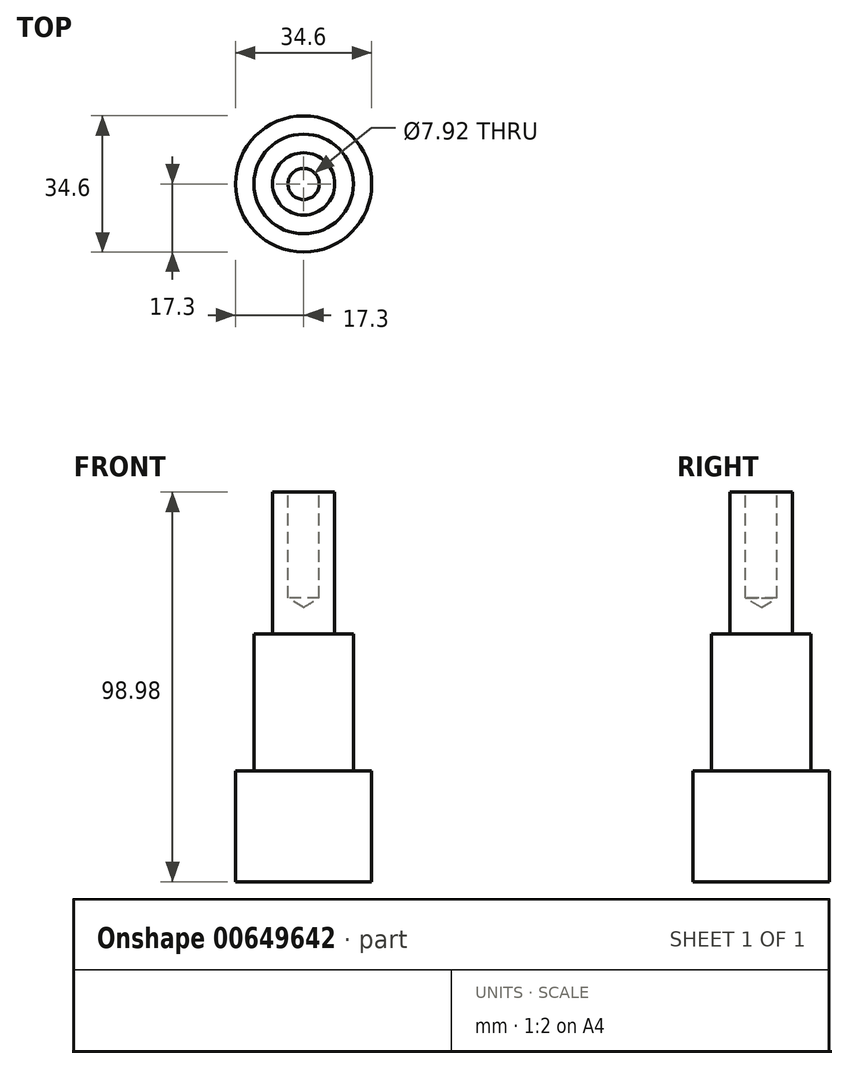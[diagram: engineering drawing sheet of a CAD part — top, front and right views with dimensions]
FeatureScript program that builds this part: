
annotation { "Feature Type Name" : "Feature", "Feature Type Description" : "" }
export const myFeature = defineFeature(function(context is Context, id is Id, definition is map)
    precondition{}
    {
        {
            var Q0;
            Q0=qCreatedBy(makeId("Top.planeOp"),FACE);
            var sketch = newSketch(context, id + "F0", { "sketchPlane" : qUnion([Q0])});
            skCircle(sketch, "E0", {"center": v(0, 0) * mm, "radius": 17.3 * mm});
            skSolve(sketch);
        }
        {
            var Q0;
            Q0=makeQuery(id+"F0.imprint","IMPRINT",FACE,{"disambiguationData":[TD([[makeQuery(id+"F0.imprint","IMPRINT",EDGE,{"derivedFrom":sQuery(id+"F0.wireOp",EDGE,"E0")}),1.0]])]});
            extrude(context, id + "F1", {"entities" : qUnion([Q0]), "depth" : 28.1 * mm, "offsetDistance" : 25 * mm});
        }
        {
            var Q0;
            Q0=makeQuery(id+"F1.opExtrude","CAP_FACE",FACE,{"disambiguationData":[OSD([sQuery(id+"F0.wireOp",EDGE,"E0")])],"isStart":false});
            var sketch = newSketch(context, id + "F2", { "sketchPlane" : qUnion([Q0])});
            skCircle(sketch, "E1", {"center": v(0, 0) * mm, "radius": 12.66 * mm});
            skSolve(sketch);
        }
        {
            var Q0;
            Q0 = qSketchRegion(id + "F2", true);
            extrude(context, id + "F3", {"entities" : qUnion([Q0]), "operationType" : NewBodyOperationType.ADD, "depth" : 34.88 * mm, "offsetDistance" : 25 * mm});
        }
        {
            var Q0;
            Q0=makeQuery(id+"F3.opExtrude","CAP_FACE",FACE,{"disambiguationData":[OSD([sQuery(id+"F2.wireOp",EDGE,"E1")])],"isStart":false});
            var sketch = newSketch(context, id + "F4", { "sketchPlane" : qUnion([Q0])});
            skCircle(sketch, "E2", {"center": v(0, 0) * mm, "radius": 7.9 * mm});
            skSolve(sketch);
        }
        {
            var Q0;
            Q0=makeQuery(id+"F4.imprint","IMPRINT",FACE,{"disambiguationData":[TD([[makeQuery(id+"F4.imprint","IMPRINT",EDGE,{"derivedFrom":sQuery(id+"F4.wireOp",EDGE,"E2")}),1.0]])]});
            var Q1;
            Q1=sQuery(id+"F4.wireOp",EDGE,"E2");
            extrude(context, id + "F5", {"entities" : qUnion([Q0]), "surfaceEntities" : qUnion([Q1]), "depth" : 36 * mm, "offsetDistance" : 25 * mm});
        }
        {
            var Q0;
            Q0=makeQuery(id+"F5.opExtrude","CAP_FACE",FACE,{"disambiguationData":[OSD([sQuery(id+"F4.wireOp",EDGE,"E2")])],"isStart":false});
            var sketch = newSketch(context, id + "F6", { "sketchPlane" : qUnion([Q0])});
            skCircle(sketch, "E3", {"center": v(0, 0) * mm, "radius": 3.96 * mm});
            skSolve(sketch);
        }
        {
            var Q0;
            Q0=sQuery(id+"F6.wireOp",VERTEX,"E3.center");
            var Q1;
            Q1=makeQuery(id+"F5.opExtrude","SWEPT_BODY",BODY,{"disambiguationData":[OSD([sQuery(id+"F4.wireOp",EDGE,"E2")])]});
            hole(context, id + "F7", {"style" : HoleStyle.SIMPLE, "endStyle" : HoleEndStyle.BLIND, "holeDiameter" : 7.92 * mm, "majorDiameter" : 5 * mm, "holeDepth" : 26.9 * mm, "isTappedThrough" : true, "tappedDepth" : 12 * mm, "tapClearance" : 3, "startFromSketch" : true, "locations" : qUnion([Q0]), "scope" : qUnion([Q1])});
        }
    });
